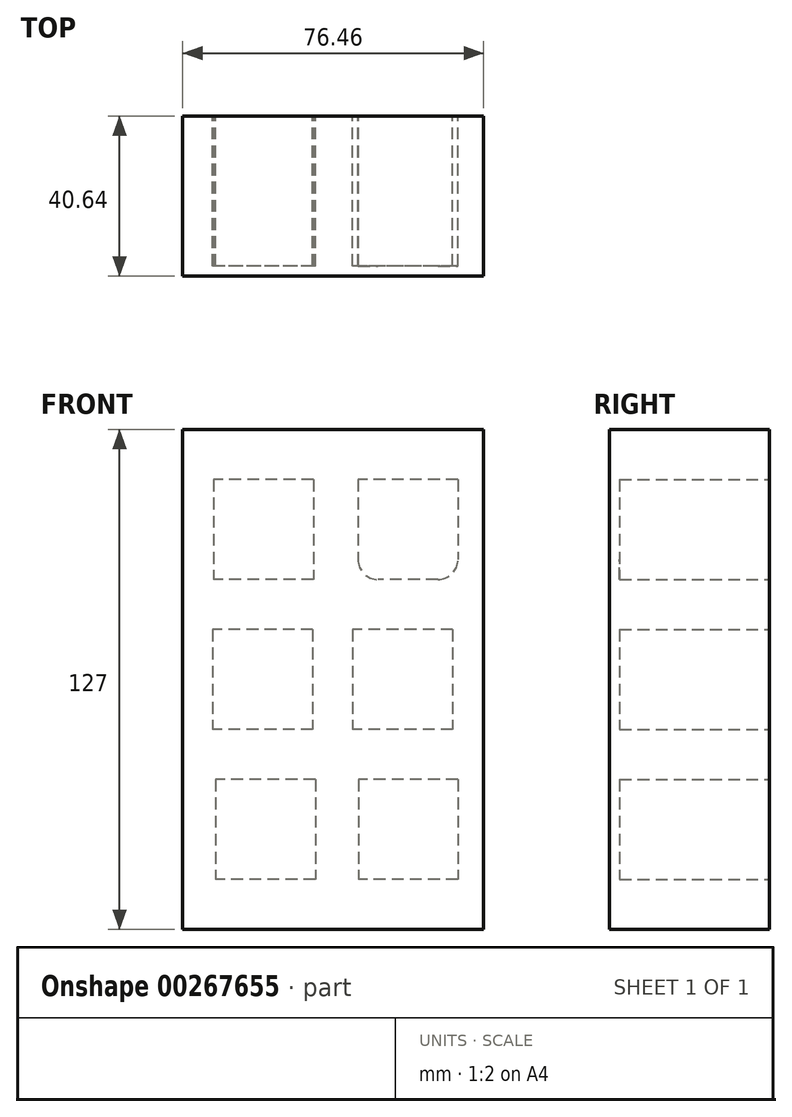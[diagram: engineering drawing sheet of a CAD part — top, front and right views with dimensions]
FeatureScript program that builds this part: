
annotation { "Feature Type Name" : "Feature", "Feature Type Description" : "" }
export const myFeature = defineFeature(function(context is Context, id is Id, definition is map)
    precondition{}
    {
        {
            var Q0;
            Q0=qCreatedBy(makeId("Front.planeOp"),FACE);
            var sketch = newSketch(context, id + "F0", { "sketchPlane" : qUnion([Q0])});
            skLineSegment(sketch, "E0.bottom", {"start": v(38.23, 63.5) * mm, "end": v(-38.23, 63.5) * mm});
            skLineSegment(sketch, "E0.top", {"start": v(38.23, -63.5) * mm, "end": v(-38.23, -63.5) * mm});
            skLineSegment(sketch, "E0.left", {"start": v(38.23, 63.5) * mm, "end": v(38.23, -63.5) * mm});
            skLineSegment(sketch, "E0.right", {"start": v(-38.23, 63.5) * mm, "end": v(-38.23, -63.5) * mm});
            skSolve(sketch);
        }
        {
            var Q0;
            Q0=makeQuery(id+"F0.imprint","IMPRINT",FACE,{"disambiguationData":[TD([[makeQuery(id+"F0.imprint","IMPRINT",EDGE,{"derivedFrom":sQuery(id+"F0.wireOp",EDGE,"E0.bottom")}),1.0]])]});
            var sketch = newSketch(context, id + "F1", { "sketchPlane" : qUnion([Q0])});
            skLineSegment(sketch, "E1.bottom", {"start": v(-5, 50.8) * mm, "end": v(-30.4, 50.8) * mm});
            skLineSegment(sketch, "E1.top", {"start": v(-5, 25.4) * mm, "end": v(-30.4, 25.4) * mm});
            skLineSegment(sketch, "E1.left", {"start": v(-5, 50.8) * mm, "end": v(-5, 25.4) * mm});
            skLineSegment(sketch, "E1.right", {"start": v(-30.4, 50.8) * mm, "end": v(-30.4, 25.4) * mm});
            skPoint(sketch, "E1.middle", {"position": v(-17.7, 38.1) * mm});
            skLineSegment(sketch, "E2.bottom", {"start": v(31.7, 50.8) * mm, "end": v(6.3, 50.8) * mm});
            skLineSegment(sketch, "E2.top", {"start": v(31.7, 25.4) * mm, "end": v(6.3, 25.4) * mm});
            skLineSegment(sketch, "E2.left", {"start": v(31.7, 50.8) * mm, "end": v(31.7, 25.4) * mm});
            skLineSegment(sketch, "E2.right", {"start": v(6.3, 50.8) * mm, "end": v(6.3, 25.4) * mm});
            skPoint(sketch, "E2.middle", {"position": v(19, 38.1) * mm});
            skLineSegment(sketch, "E3.bottom", {"start": v(30.37, 12.7) * mm, "end": v(4.97, 12.7) * mm});
            skLineSegment(sketch, "E3.top", {"start": v(30.37, -12.7) * mm, "end": v(4.97, -12.7) * mm});
            skLineSegment(sketch, "E3.left", {"start": v(30.37, 12.7) * mm, "end": v(30.37, -12.7) * mm});
            skLineSegment(sketch, "E3.right", {"start": v(4.97, 12.7) * mm, "end": v(4.97, -12.7) * mm});
            skPoint(sketch, "E3.middle", {"position": v(17.67, 0) * mm});
            skLineSegment(sketch, "E4.bottom", {"start": v(-5.2, 12.7) * mm, "end": v(-30.6, 12.7) * mm});
            skLineSegment(sketch, "E4.top", {"start": v(-5.2, -12.7) * mm, "end": v(-30.6, -12.7) * mm});
            skLineSegment(sketch, "E4.left", {"start": v(-5.2, 12.7) * mm, "end": v(-5.2, -12.7) * mm});
            skLineSegment(sketch, "E4.right", {"start": v(-30.6, 12.7) * mm, "end": v(-30.6, -12.7) * mm});
            skPoint(sketch, "E4.middle", {"position": v(-17.9, 0) * mm});
            skLineSegment(sketch, "E5.bottom", {"start": v(-4.5, -25.4) * mm, "end": v(-29.9, -25.4) * mm});
            skLineSegment(sketch, "E5.top", {"start": v(-4.5, -50.8) * mm, "end": v(-29.9, -50.8) * mm});
            skLineSegment(sketch, "E5.left", {"start": v(-4.5, -25.4) * mm, "end": v(-4.5, -50.8) * mm});
            skLineSegment(sketch, "E5.right", {"start": v(-29.9, -25.4) * mm, "end": v(-29.9, -50.8) * mm});
            skPoint(sketch, "E5.middle", {"position": v(-17.2, -38.1) * mm});
            skLineSegment(sketch, "E6.bottom", {"start": v(31.7, -25.4) * mm, "end": v(6.48, -25.4) * mm});
            skLineSegment(sketch, "E6.top", {"start": v(31.7, -50.8) * mm, "end": v(6.48, -50.8) * mm});
            skLineSegment(sketch, "E6.left", {"start": v(31.7, -25.4) * mm, "end": v(31.7, -50.8) * mm});
            skLineSegment(sketch, "E6.right", {"start": v(6.48, -25.4) * mm, "end": v(6.48, -50.8) * mm});
            skPoint(sketch, "E6.middle", {"position": v(19.1, -38.1) * mm});
            skSolve(sketch);
        }
        {
            var Q0;
            Q0=makeQuery(id+"F0.imprint","IMPRINT",FACE,{"disambiguationData":[TD([[makeQuery(id+"F0.imprint","IMPRINT",EDGE,{"derivedFrom":sQuery(id+"F0.wireOp",EDGE,"E0.bottom")}),1.0]])]});
            extrude(context, id + "F2", {"entities" : qUnion([Q0]), "depth" : 40.64 * mm});
        }
        {
            var Q0;
            Q0 = qSketchRegion(id + "F1", true);
            extrude(context, id + "F3", {"entities" : qUnion([Q0]), "operationType" : NewBodyOperationType.REMOVE, "depth" : 38.1 * mm});
        }
        {
            var Q0;
            Q0=makeQuery(id+"F3.boolean.opBoolean","COPY",EDGE,{"derivedFrom":makeQuery(id+"F3.opExtrude","SWEPT_EDGE",EDGE,{"disambiguationData":[OSD([sQuery(id+"F1.wireOp",EDGE,"E2.top"),sQuery(id+"F1.wireOp",EDGE,"E2.right")])]})});
            var Q1;
            Q1=makeQuery(id+"F3.boolean.opBoolean","COPY",EDGE,{"derivedFrom":makeQuery(id+"F3.opExtrude","SWEPT_EDGE",EDGE,{"disambiguationData":[OSD([sQuery(id+"F1.wireOp",EDGE,"E2.top"),sQuery(id+"F1.wireOp",EDGE,"E2.left")])]})});
            fillet(context, id + "F4", {"entities" : qUnion([Q0, Q1]), "radius" : 5.08 * mm, "tangentPropagation" : true, "allowEdgeOverflow" : false});
        }
    });
